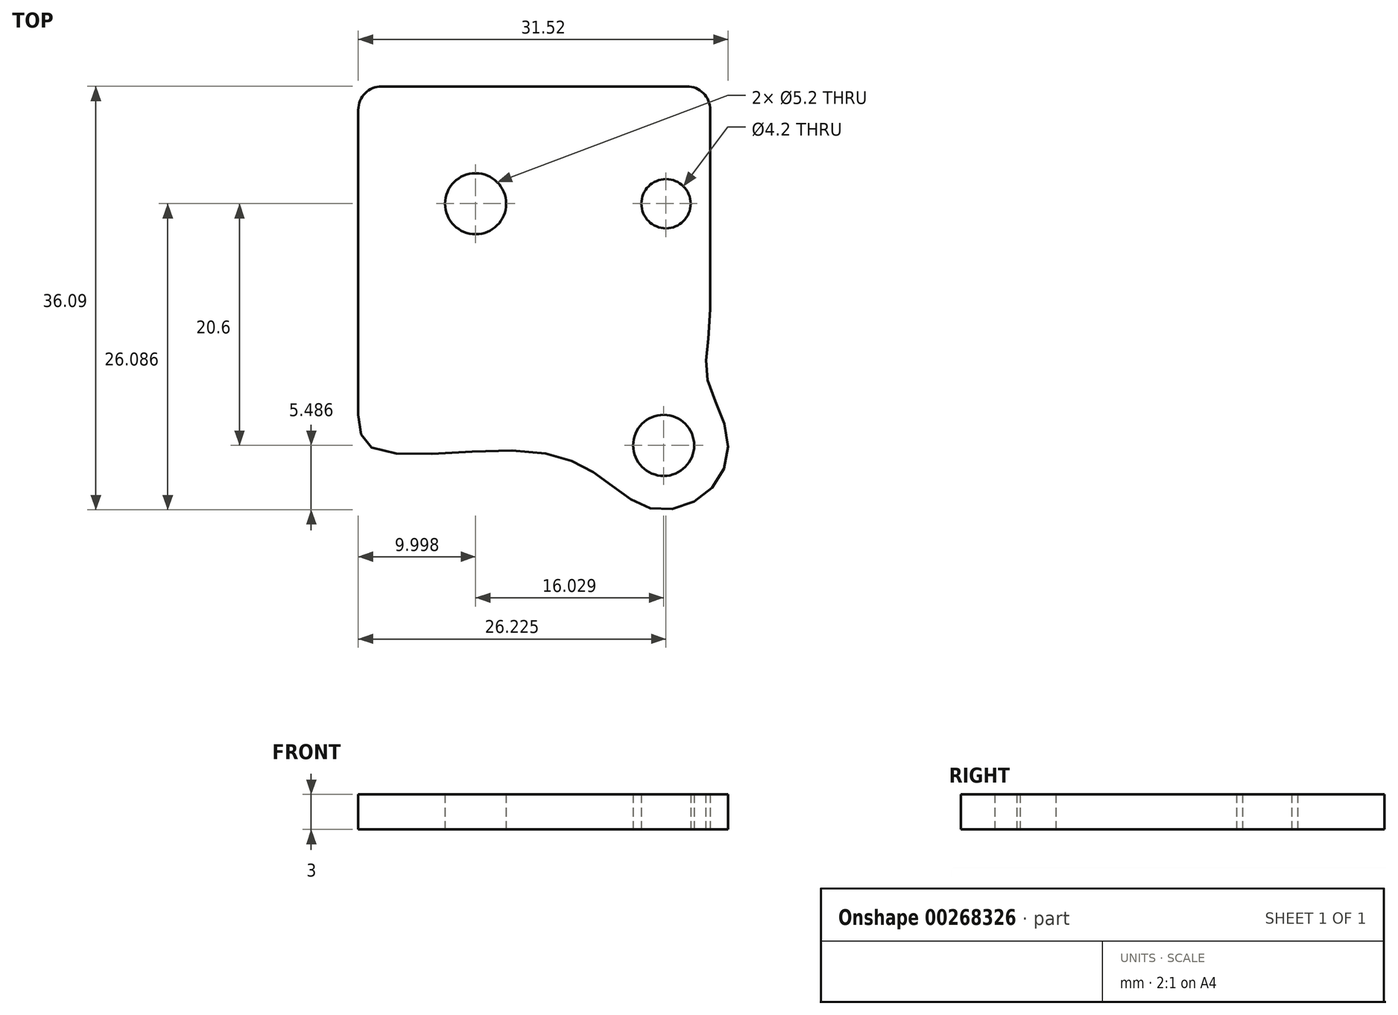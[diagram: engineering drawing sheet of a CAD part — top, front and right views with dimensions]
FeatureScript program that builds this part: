
annotation { "Feature Type Name" : "Feature", "Feature Type Description" : "" }
export const myFeature = defineFeature(function(context is Context, id is Id, definition is map)
    precondition{}
    {
        {
            var Q0;
            Q0=qCreatedBy(makeId("Top.planeOp"),FACE);
            var sketch = newSketch(context, id + "F0", { "sketchPlane" : qUnion([Q0])});
            skLineSegment(sketch, "E0.bottom", {"start": v(-13.65, 7.9) * mm, "end": v(12.35, 7.9) * mm});
            skLineSegment(sketch, "E0.left", {"start": v(-15.65, 5.9) * mm, "end": v(-15.65, -20.1) * mm});
            skLineSegment(sketch, "E0.right", {"start": v(14.35, 5.9) * mm, "end": v(14.35, -11.17) * mm});
            skCircle(sketch, "E1", {"center": v(10.57, -2.1) * mm, "radius": 2.1 * mm});
            skCircle(sketch, "E2", {"center": v(-5.65, -2.1) * mm, "radius": 2.6 * mm});
            skCircle(sketch, "E3", {"center": v(10.38, -22.7) * mm, "radius": 2.6 * mm});
            skPoint(sketch, "E4.orphan", {"position": v(14.35, -22.1) * mm});
            skPoint(sketch, "E5.visualSharp", {"position": v(-15.65, 7.9) * mm});
            skArc(sketch, "E5.filletArc", {"start": v(-13.65, 7.9) * mm, "mid": v(-15.07, 7.32) * mm, "end": v(-15.65, 5.9) * mm});
            skPoint(sketch, "E6.visualSharp", {"position": v(14.35, 7.9) * mm});
            skArc(sketch, "E6.filletArc", {"start": v(14.35, 5.9) * mm, "mid": v(13.76, 7.32) * mm, "end": v(12.35, 7.9) * mm});
            skPoint(sketch, "E7.visualSharp", {"position": v(14.35, -11.09) * mm});
            skPoint(sketch, "E8.visualSharp", {"position": v(-15.65, -22.1) * mm});
            skPoint(sketch, "E9.visualSharp", {"position": v(6.78, -30.02) * mm});
            skFitSpline(sketch, "E10", {"points": [v(-15.65, -20.1) * mm, v(-14.35, -22.97) * mm, v(-1.46, -23.18) * mm, v(5.2, -25.54) * mm, v(9.52, -28.1) * mm, v(14.22, -26.6) * mm, v(15.82, -22.08) * mm, v(14.06, -16.86) * mm, v(14.35, -11.09) * mm], "startDerivative": vector(2.52, -42.95) * mm, "endDerivative": vector(0.45, 68.55) * mm});
            skLineSegment(sketch, "E11", {"start": v(-5.65, -2.1) * mm, "end": v(36.16, -2.1) * mm, "construction": true});
            skLineSegment(sketch, "E12", {"start": v(36.16, -2.1) * mm, "end": v(36.16, -12.1) * mm, "construction": true});
            skLineSegment(sketch, "E13", {"start": v(36.16, -12.1) * mm, "end": v(-5.65, -12.1) * mm, "construction": true});
            skLineSegment(sketch, "E14", {"start": v(-5.65, -12.1) * mm, "end": v(-5.65, -2.1) * mm, "construction": true});
            skCircle(sketch, "E15", {"center": v(10.38, -22.7) * mm, "radius": 5.48 * mm, "construction": true});
            skSolve(sketch);
        }
        {
            var Q0;
            Q0=qSketchRegion(id+"F0",true);
            extrude(context, id + "F1", {"entities" : qUnion([Q0]), "depth" : 3 * mm});
        }
    });
